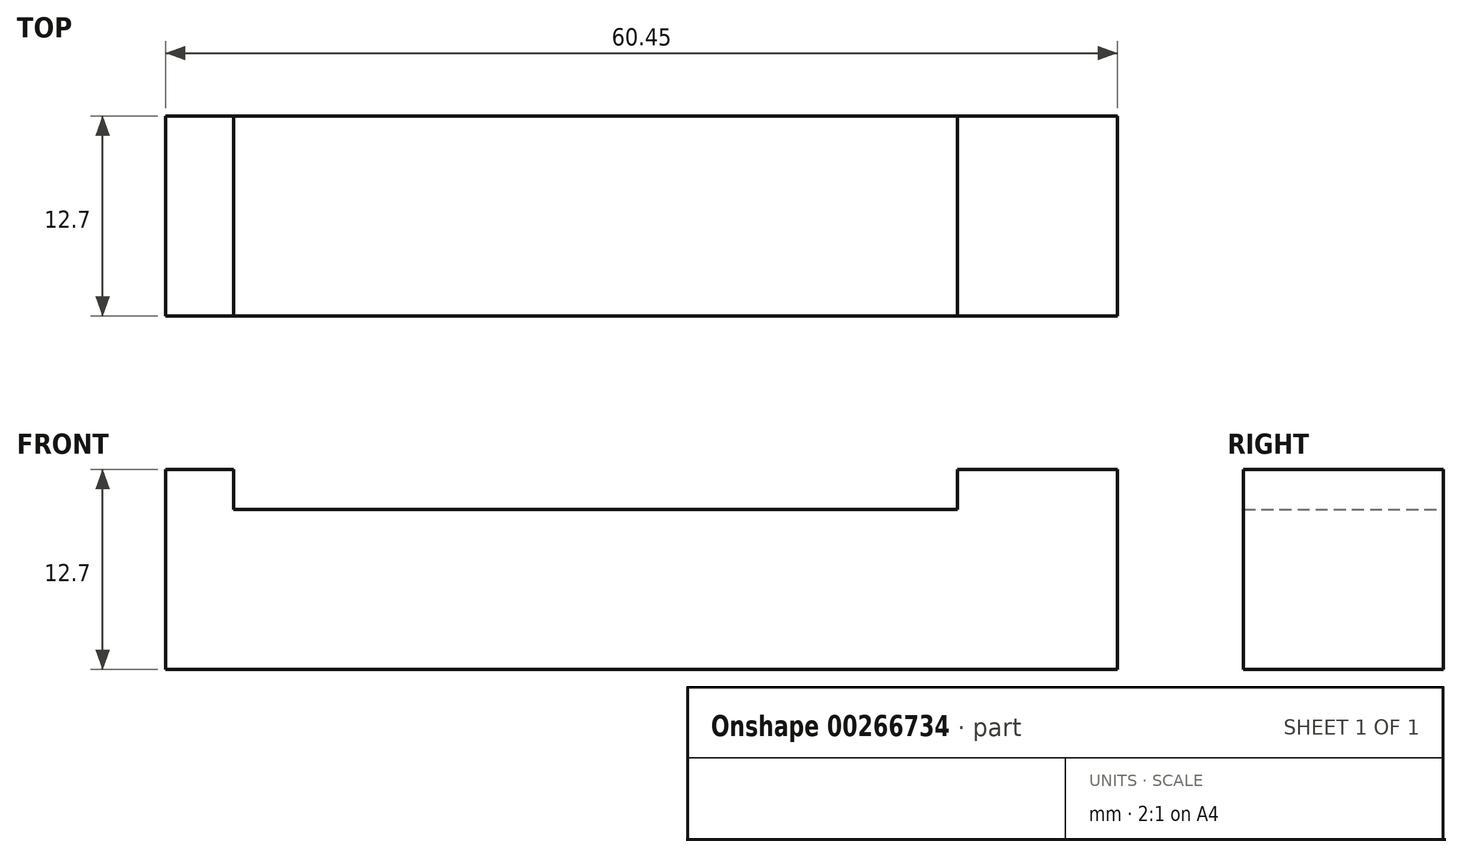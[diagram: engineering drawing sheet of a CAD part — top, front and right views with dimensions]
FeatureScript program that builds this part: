
annotation { "Feature Type Name" : "Feature", "Feature Type Description" : "" }
export const myFeature = defineFeature(function(context is Context, id is Id, definition is map)
    precondition{}
    {
        {
            var Q0;
            Q0=qCreatedBy(makeId("Front.planeOp"),FACE);
            var sketch = newSketch(context, id + "F0", { "sketchPlane" : qUnion([Q0])});
            skLineSegment(sketch, "E0", {"start": v(0, 0) * mm, "end": v(0, 12.7) * mm});
            skLineSegment(sketch, "E1", {"start": v(0, 12.7) * mm, "end": v(10.16, 12.7) * mm});
            skLineSegment(sketch, "E2", {"start": v(10.16, 12.7) * mm, "end": v(10.16, 10.16) * mm});
            skLineSegment(sketch, "E3", {"start": v(10.16, 10.16) * mm, "end": v(56.13, 10.16) * mm});
            skLineSegment(sketch, "E4", {"start": v(56.13, 10.16) * mm, "end": v(56.13, 12.7) * mm});
            skLineSegment(sketch, "E5", {"start": v(56.13, 12.7) * mm, "end": v(66.3, 12.7) * mm});
            skLineSegment(sketch, "E6", {"start": v(66.3, 12.7) * mm, "end": v(66.3, 0) * mm});
            skLineSegment(sketch, "E7", {"start": v(66.3, 0) * mm, "end": v(0, 0) * mm});
            skLineSegment(sketch, "E8", {"start": v(5.84, 15.24) * mm, "end": v(-0.5, 15.24) * mm});
            skLineSegment(sketch, "E9", {"start": v(-0.5, 15.24) * mm, "end": v(-10.88, 3.85) * mm});
            skLineSegment(sketch, "E10", {"start": v(0, 0) * mm, "end": v(-6.65, 0) * mm});
            skCircle(sketch, "E11", {"center": v(-6.65, 0) * mm, "radius": 5.72 * mm});
            skCircle(sketch, "E12", {"center": v(-6.65, 0) * mm, "radius": 3.18 * mm});
            skLineSegment(sketch, "E13", {"start": v(5.84, 15.24) * mm, "end": v(5.84, -9.4) * mm});
            skLineSegment(sketch, "E14", {"start": v(5.84, -9.4) * mm, "end": v(-8.18, -5.5) * mm});
            skSolve(sketch);
        }
        {
            var Q0;
            {var subQ0=sQuery(id+"F0.wireOp",EDGE,"E2");Q0=makeQuery(id+"F0.imprint","IMPRINT",FACE,{"disambiguationData":[TD([[makeQuery(id+"F0.imprint","IMPRINT",EDGE,{"derivedFrom":subQ0}),-1.0]])]});}
            extrude(context, id + "F1", {"entities" : qUnion([Q0]), "endBound" : BoundingType.SYMMETRIC, "depth" : 12.7 * mm});
        }
    });
